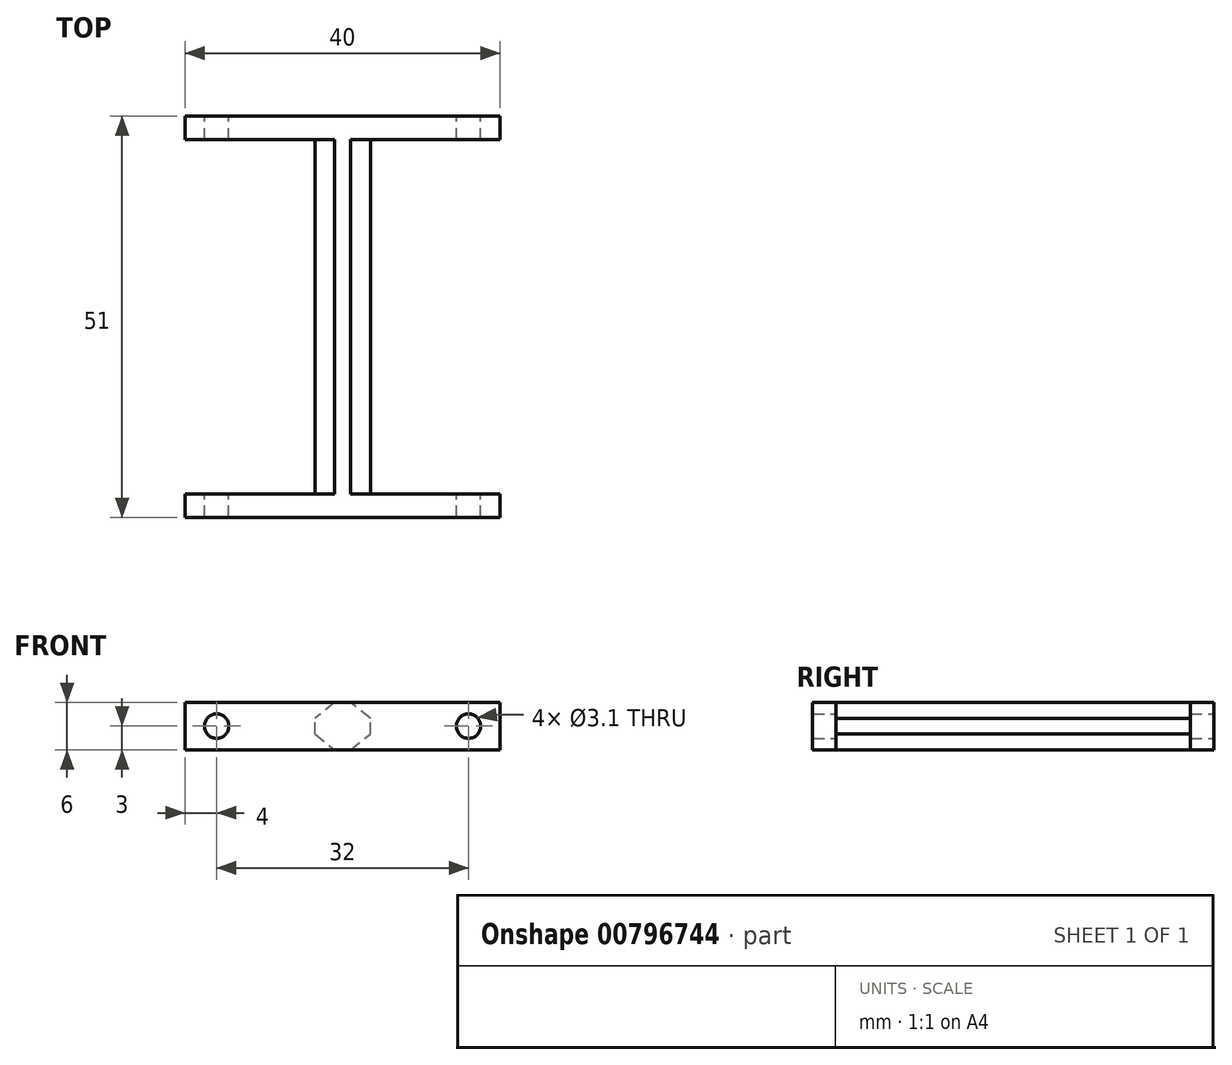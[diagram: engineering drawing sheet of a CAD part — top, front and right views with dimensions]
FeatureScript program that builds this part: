
annotation { "Feature Type Name" : "Feature", "Feature Type Description" : "" }
export const myFeature = defineFeature(function(context is Context, id is Id, definition is map)
    precondition{}
    {
        {
            var Q0;
            Q0=qCreatedBy(makeId("Front.planeOp"),FACE);
            var sketch = newSketch(context, id + "F0", { "sketchPlane" : qUnion([Q0])});
            skLineSegment(sketch, "E0.bottom", {"start": v(20, -3) * mm, "end": v(-20, -3) * mm});
            skLineSegment(sketch, "E0.top", {"start": v(20, 3) * mm, "end": v(-20, 3) * mm});
            skLineSegment(sketch, "E0.left", {"start": v(20, -3) * mm, "end": v(20, 3) * mm});
            skLineSegment(sketch, "E0.right", {"start": v(-20, -3) * mm, "end": v(-20, 3) * mm});
            skLineSegment(sketch, "E1", {"start": v(0, 0) * mm, "end": v(-20, 0) * mm, "construction": true});
            skLineSegment(sketch, "E2", {"start": v(0, 3) * mm, "end": v(0, 0) * mm, "construction": true});
            skSolve(sketch);
        }
        {
            var Q0;
            Q0 = qSketchRegion(id + "F0", true);
            extrude(context, id + "F1", {"entities" : qUnion([Q0]), "depth" : 3 * mm, "offsetDistance" : 25 * mm});
        }
        {
            var Q0;
            Q0=makeQuery(id+"F1.opExtrude","CAP_FACE",FACE,{"disambiguationData":[OSD([sQuery(id+"F0.wireOp",EDGE,"E0.bottom"),sQuery(id+"F0.wireOp",EDGE,"E0.top"),sQuery(id+"F0.wireOp",EDGE,"E0.left"),sQuery(id+"F0.wireOp",EDGE,"E0.right")])],"isStart":false});
            var sketch = newSketch(context, id + "F2", { "sketchPlane" : qUnion([Q0])});
            skLineSegment(sketch, "E3.left", {"start": v(3.53, -1) * mm, "end": v(3.53, 1) * mm});
            skLineSegment(sketch, "E3.right", {"start": v(-3.53, -1) * mm, "end": v(-3.53, 1) * mm});
            skPoint(sketch, "E3.middle", {"position": v(0, 0) * mm});
            skLineSegment(sketch, "E4.bottom", {"start": v(1, 3) * mm, "end": v(-1, 3) * mm});
            skLineSegment(sketch, "E4.top", {"start": v(1, -3) * mm, "end": v(-1, -3) * mm});
            skLineSegment(sketch, "E5", {"start": v(-3.53, -1) * mm, "end": v(-1, -3) * mm});
            skLineSegment(sketch, "E6", {"start": v(1, -3) * mm, "end": v(3.53, -1) * mm});
            skLineSegment(sketch, "E7", {"start": v(3.53, 1) * mm, "end": v(1, 3) * mm});
            skLineSegment(sketch, "E8", {"start": v(-1, 3) * mm, "end": v(-3.53, 1) * mm});
            skSolve(sketch);
        }
        {
            var Q0;
            Q0 = qSketchRegion(id + "F2", true);
            extrude(context, id + "F3", {"entities" : qUnion([Q0]), "operationType" : NewBodyOperationType.ADD, "depth" : 45 * mm, "offsetDistance" : 25 * mm});
        }
        {
            var Q0;
            Q0=makeQuery(id+"F3.opExtrude","CAP_FACE",FACE,{"disambiguationData":[OSD([sQuery(id+"F2.wireOp",EDGE,"E3.bottom"),sQuery(id+"F2.wireOp",EDGE,"E3.top"),sQuery(id+"F2.wireOp",EDGE,"E3.left"),sQuery(id+"F2.wireOp",EDGE,"E3.right")])],"isStart":false});
            var sketch = newSketch(context, id + "F4", { "sketchPlane" : qUnion([Q0])});
            skLineSegment(sketch, "E9.bottom", {"start": v(-20, 3) * mm, "end": v(20, 3) * mm});
            skLineSegment(sketch, "E9.top", {"start": v(-20, -3) * mm, "end": v(20, -3) * mm});
            skLineSegment(sketch, "E9.left", {"start": v(-20, 3) * mm, "end": v(-20, -3) * mm});
            skLineSegment(sketch, "E9.right", {"start": v(20, 3) * mm, "end": v(20, -3) * mm});
            skLineSegment(sketch, "E10", {"start": v(0, 0) * mm, "end": v(0, 3) * mm, "construction": true});
            skLineSegment(sketch, "E11", {"start": v(0, 0) * mm, "end": v(20, 0) * mm, "construction": true});
            skSolve(sketch);
        }
        {
            var Q0;
            Q0 = qSketchRegion(id + "F4", true);
            extrude(context, id + "F5", {"entities" : qUnion([Q0]), "operationType" : NewBodyOperationType.ADD, "depth" : 3 * mm, "offsetDistance" : 25 * mm});
        }
        {
            var Q0;
            Q0=makeQuery(id+"F1.opExtrude","CAP_FACE",FACE,{"disambiguationData":[OSD([sQuery(id+"F0.wireOp",EDGE,"E0.bottom"),sQuery(id+"F0.wireOp",EDGE,"E0.top"),sQuery(id+"F0.wireOp",EDGE,"E0.left"),sQuery(id+"F0.wireOp",EDGE,"E0.right")])],"isStart":true});
            var sketch = newSketch(context, id + "F6", { "sketchPlane" : qUnion([Q0])});
            skCircle(sketch, "E12", {"center": v(-16, 0) * mm, "radius": 1.55 * mm});
            skCircle(sketch, "E13", {"center": v(16, 0) * mm, "radius": 1.55 * mm});
            skLineSegment(sketch, "E14", {"start": v(-20, 3) * mm, "end": v(20, -3) * mm, "construction": true});
            skLineSegment(sketch, "E15", {"start": v(0, 0) * mm, "end": v(0, -7.07) * mm, "construction": true});
            skSolve(sketch);
        }
        {
            var Q0;
            Q0 = qSketchRegion(id + "F6", true);
            extrude(context, id + "F7", {"entities" : qUnion([Q0]), "operationType" : NewBodyOperationType.REMOVE, "endBound" : BoundingType.THROUGH_ALL, "oppositeDirection" : true, "depth" : 25 * mm, "offsetDistance" : 25 * mm});
        }
    });
